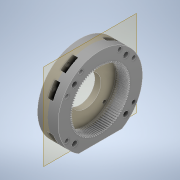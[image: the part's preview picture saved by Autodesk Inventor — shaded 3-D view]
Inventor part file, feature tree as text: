
AUTODESK INVENTOR PART (.ipt)
format: ipt  version: 2022 (Build 260153000, 153)  size: 725,504 bytes
history: mixed  units: in
note: dims shown in document units (in); Inventor stores cm internally (conversion verified against a paired STEP export)
features: sketch x4, extrude x3, plane x1, hole x1, other x1, imported_body x1
ambient origin geometry x8: Origin, YZ Plane, XZ Plane, XY Plane, X Axis, Y Axis, Z Axis, Center Point
bodies: Solid1 (imported_parasolid)
feature tree (11):
  extrude  "Extrusion1"  Depth=0.3937in TaperAngle=0.0deg
  extrude  "Extrusion2"  Depth=0.3937in TaperAngle=0.0deg
  plane  "Work Plane1"
  extrude  "Extrusion3"  Depth=0.1772in TaperAngle=0.0deg
  hole  "Hole1"  [1 undecoded]
  sketch  "Sketch2"  dims[d1=1.5748in d3=360.0deg d5=0.3937in d6=0.0in]
  sketch  "Sketch3"  dims[d7=1.5748in d9=360.0deg d11=0.3937in d12=0.0in]
  sketch  "Sketch4"  dims[d19=1.5748in d21=360.0deg d23=0.1772in d24=0.0in]
  sketch  "Sketch5"  dims[d25=0.1378in d26=0.2362in d27=0.1969in d28=0.1181in d29=90.0deg d30=0.315in d31=0.8108in d8=0.0344in]
  other  "96_Teeth_Gear.STEP"
  imported_body  NMx_Import_Brep_tag  [imported B-rep: ~453 faces, bbox_mm=[17.0, 62.865012, 65.730025]]
note: 1 required parameter value undecoded (feature->parameter linkage not recoverable at this tier; creation-order binding heuristic only, values carry confidence <= 0.55)
